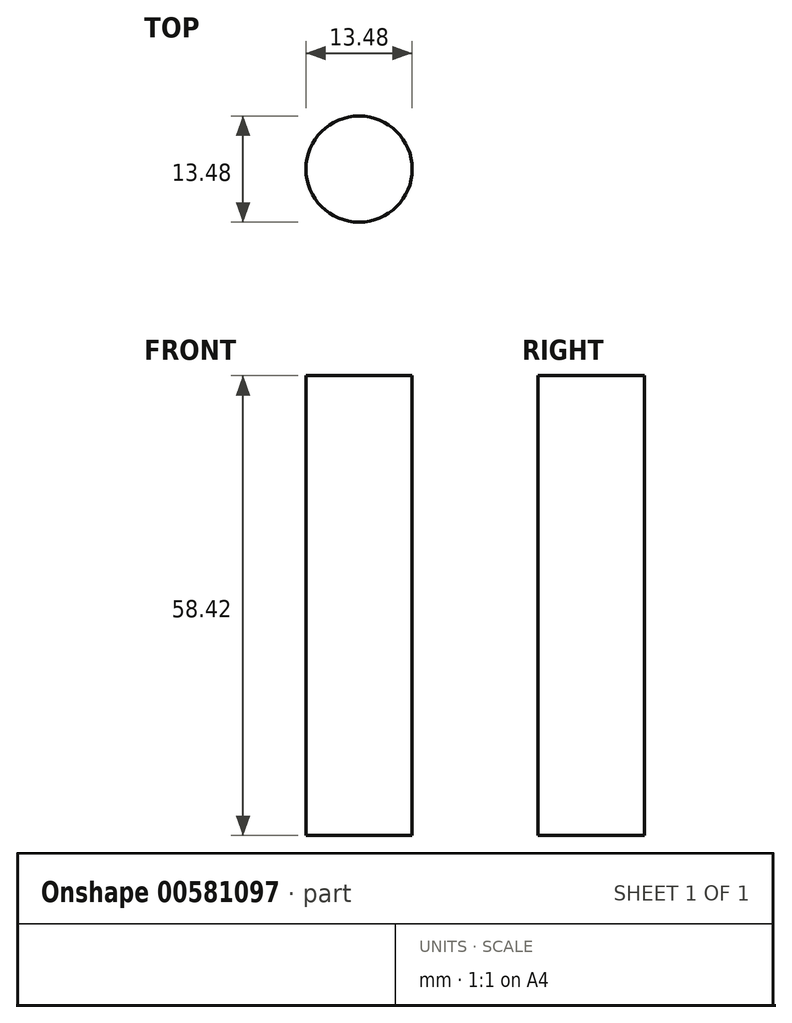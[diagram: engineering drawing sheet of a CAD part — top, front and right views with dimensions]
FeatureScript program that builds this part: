
annotation { "Feature Type Name" : "Feature", "Feature Type Description" : "" }
export const myFeature = defineFeature(function(context is Context, id is Id, definition is map)
    precondition{}
    {
        {
            var Q0;
            Q0=qCreatedBy(makeId("Top.planeOp"),FACE);
            var sketch = newSketch(context, id + "F0", { "sketchPlane" : qUnion([Q0])});
            skCircle(sketch, "E0", {"center": v(0, 0) * mm, "radius": 6.74 * mm});
            skCircle(sketch, "E1.cCircle", {"center": v(0, 0) * mm, "radius": 6.74 * mm, "construction": true});
            skPoint(sketch, "E1.0.midPoint", {"position": v(6.74, 0) * mm});
            skCircle(sketch, "E2", {"center": v(3.89, 0) * mm, "radius": 2.86 * mm});
            skCircle(sketch, "E3", {"center": v(-1.94, 3.37) * mm, "radius": 2.86 * mm});
            skCircle(sketch, "E4", {"center": v(-1.94, -3.37) * mm, "radius": 2.86 * mm});
            skCircle(sketch, "E5", {"center": v(-1.94, 3.37) * mm, "radius": 3.53 * mm});
            skCircle(sketch, "E6", {"center": v(3.89, 0) * mm, "radius": 3.53 * mm});
            skCircle(sketch, "E7", {"center": v(-1.94, -3.37) * mm, "radius": 3.53 * mm});
            skSolve(sketch);
        }
        {
            var Q0;
            Q0=sQuery(id+"F0.wireOp",EDGE,"E0");
            extrude(context, id + "F1", {"bodyType" : ToolBodyType.SURFACE, "surfaceEntities" : qUnion([Q0]), "depth" : 58.42 * mm, "offsetDistance" : 25.4 * mm});
        }
    });
